# Revit family: QF_ELECTROLUXPROFESSIONAL_1LSNJ9_IC64825LF_E
name_source: partatom
category: Attrezzature speciali
units: mm (PartAtom-declared; Revit-internal decimal feet)

## family parameters
Basato su piano di lavoro = No
Condiviso = No
Punto di calcolo locali = No
Quota connettore circolare = Usa diametro
Sempre verticale = Sì
Taglio con vuoti quando caricato = No
Tipo di parte = Normale

## types (5) — shared parameters
Cycle = 50 Hz
Depth Actual = 1110 mm
Height Actual = 1270 mm  [stored 4.16667 ft]
Latent Heat Output = 0.0
Length Actual = 3205 mm
Modello = IC64825LF
Phase = 3
Produttore = Electrolux Professional
Sensible Heat Output = 0.0
URL = www.electroluxprofessional.com
Volts = 400 V
Weight = 875
zero-valued in all types: Gas KW, Prospetto di default, Steam Pounds per Hour

## per-type parameters (varying)
| type | Descrizione | Item Number | Watts |
| 9882030318 | IRONER CYLINDER IC64825LF LENGTH FOLDING 2540MM EL. CE 400/50/3 6MM SST CYL. ML DIAMMS | 1LT6DH | 44600 W |
| 9882030170 | IRONER CYLINDER IC64825LF LENGTH FOLDING 2540MM PERFORMANCE EL. CE 400/50/3 DUBIXIUM ML VAC.FEED.TABLE DIAMMS | 1LSPED | 446000 W |
| 9882030305 | IRONER CYLINDER IC64825LF LENGTH FOLDING 2540MM SUPERIOR EL. CE 400/50/3 DUBIXIUM FR FEED ALONE VAC.FEED.TABLE ANTISTATI | 1LT671 | 446000 W |
| 9882030169 | IRONER CYLINDER IC64825LF LENGTH FOLDING 2540MM PERFORMANCE EL. CE 400/50/3 DUBIXIUM FR VAC.FEED.TABLE DIAMMS | 1LD05T | 446000 W |
| 9882030272 | IRONER CYLINDER IC64825LF LENGTH FOLDING 2540MM EL. CE 400/50/3 DUBIXIUM SE, DK, FI VAC.FEED.TABLE ANTISTATIC DIAMMS | 1LSRJD | 446000 W |

note: [stored X ft] marks values corroborated as IEEE doubles in the binary element streams (Revit-internal decimal feet)

## geometry (parser evidence)
native form markers: Sweep x11
no freeform markers — native parametric forms only
